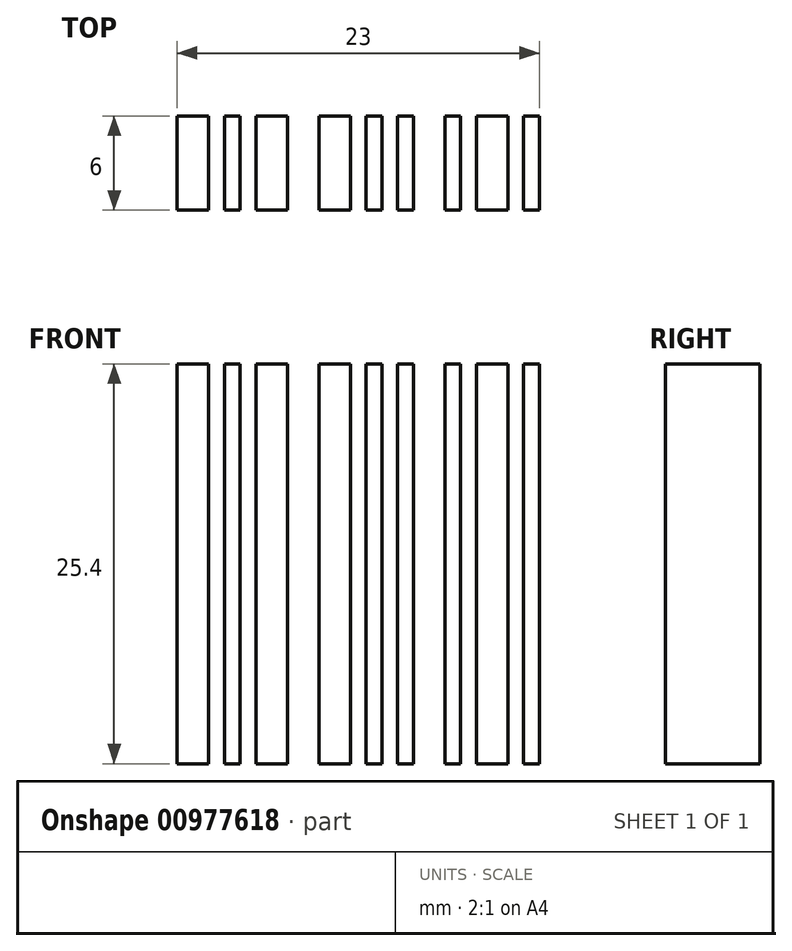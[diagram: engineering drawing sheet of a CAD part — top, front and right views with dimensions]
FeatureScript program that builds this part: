
annotation { "Feature Type Name" : "Feature", "Feature Type Description" : "" }
export const myFeature = defineFeature(function(context is Context, id is Id, definition is map)
    precondition{}
    {
        {
            var Q0;
            Q0=qCreatedBy(makeId("Top.planeOp"),FACE);
            var sketch = newSketch(context, id + "F0", { "sketchPlane" : qUnion([Q0])});
            skLineSegment(sketch, "E0.bottom", {"start": v(0, 0) * mm, "end": v(2, 0) * mm});
            skLineSegment(sketch, "E0.top", {"start": v(0, 6) * mm, "end": v(2, 6) * mm});
            skLineSegment(sketch, "E0.left", {"start": v(0, 0) * mm, "end": v(0, 6) * mm});
            skLineSegment(sketch, "E0.right", {"start": v(2, 0) * mm, "end": v(2, 6) * mm});
            skLineSegment(sketch, "E1", {"start": v(0, -3.5) * mm, "end": v(3, -3.5) * mm});
            skLineSegment(sketch, "E2", {"start": v(3, -3.5) * mm, "end": v(4, -3.5) * mm});
            skLineSegment(sketch, "E3", {"start": v(4, -3.5) * mm, "end": v(5, -3.5) * mm});
            skLineSegment(sketch, "E4", {"start": v(5, -3.5) * mm, "end": v(7, -3.5) * mm});
            skLineSegment(sketch, "E5", {"start": v(7, -3.5) * mm, "end": v(9, -3.5) * mm});
            skLineSegment(sketch, "E6.bottom", {"start": v(3, 0) * mm, "end": v(4, 0) * mm});
            skLineSegment(sketch, "E6.top", {"start": v(3, 6) * mm, "end": v(4, 6) * mm});
            skLineSegment(sketch, "E6.left", {"start": v(3, 0) * mm, "end": v(3, 6) * mm});
            skLineSegment(sketch, "E6.right", {"start": v(4, 0) * mm, "end": v(4, 6) * mm});
            skLineSegment(sketch, "E7.bottom", {"start": v(5, 0) * mm, "end": v(7, 0) * mm});
            skLineSegment(sketch, "E7.top", {"start": v(5, 6) * mm, "end": v(7, 6) * mm});
            skLineSegment(sketch, "E7.left", {"start": v(5, 0) * mm, "end": v(5, 6) * mm});
            skLineSegment(sketch, "E7.right", {"start": v(7, 0) * mm, "end": v(7, 6) * mm});
            skLineSegment(sketch, "E8.bottom", {"start": v(9, 0) * mm, "end": v(9, 0) * mm});
            skLineSegment(sketch, "E9.bottom", {"start": v(9, -3.5) * mm, "end": v(11, -3.5) * mm});
            skLineSegment(sketch, "E9.top", {"start": v(9, -3.5) * mm, "end": v(11, -3.5) * mm});
            skLineSegment(sketch, "E9.left", {"start": v(9, -3.5) * mm, "end": v(9, -3.5) * mm});
            skLineSegment(sketch, "E9.right", {"start": v(11, -3.5) * mm, "end": v(11, -3.5) * mm});
            skLineSegment(sketch, "E10.bottom", {"start": v(11, -3.5) * mm, "end": v(12, -3.5) * mm});
            skLineSegment(sketch, "E10.top", {"start": v(11, -3.5) * mm, "end": v(12, -3.5) * mm});
            skLineSegment(sketch, "E10.right", {"start": v(12, -3.5) * mm, "end": v(12, -3.5) * mm});
            skLineSegment(sketch, "E11.bottom", {"start": v(12, -3.5) * mm, "end": v(13, -3.5) * mm});
            skLineSegment(sketch, "E11.top", {"start": v(12, -3.5) * mm, "end": v(13, -3.5) * mm});
            skLineSegment(sketch, "E11.right", {"start": v(13, -3.5) * mm, "end": v(13, -3.5) * mm});
            skLineSegment(sketch, "E12.bottom", {"start": v(13, -3.5) * mm, "end": v(14, -3.5) * mm});
            skLineSegment(sketch, "E12.top", {"start": v(13, -3.5) * mm, "end": v(14, -3.5) * mm});
            skLineSegment(sketch, "E12.right", {"start": v(14, -3.5) * mm, "end": v(14, -3.5) * mm});
            skLineSegment(sketch, "E13.bottom", {"start": v(9, 0) * mm, "end": v(11, 0) * mm});
            skLineSegment(sketch, "E13.top", {"start": v(9, 6) * mm, "end": v(11, 6) * mm});
            skLineSegment(sketch, "E13.left", {"start": v(9, 0) * mm, "end": v(9, 6) * mm});
            skLineSegment(sketch, "E13.right", {"start": v(11, 0) * mm, "end": v(11, 6) * mm});
            skLineSegment(sketch, "E14.bottom", {"start": v(12, 0) * mm, "end": v(13, 0) * mm});
            skLineSegment(sketch, "E14.top", {"start": v(12, 6) * mm, "end": v(13, 6) * mm});
            skLineSegment(sketch, "E14.left", {"start": v(12, 0) * mm, "end": v(12, 6) * mm});
            skLineSegment(sketch, "E14.right", {"start": v(13, 0) * mm, "end": v(13, 6) * mm});
            skLineSegment(sketch, "E15.bottom", {"start": v(14, 0) * mm, "end": v(14, 0) * mm});
            skLineSegment(sketch, "E15.top", {"start": v(14, 6) * mm, "end": v(14, 6) * mm});
            skLineSegment(sketch, "E15.left", {"start": v(14, 0) * mm, "end": v(14, 6) * mm});
            skLineSegment(sketch, "E15.right", {"start": v(14, 0) * mm, "end": v(14, 6) * mm});
            skLineSegment(sketch, "E16.bottom", {"start": v(14, 6) * mm, "end": v(15, 6) * mm});
            skLineSegment(sketch, "E16.top", {"start": v(14, 0) * mm, "end": v(15, 0) * mm});
            skLineSegment(sketch, "E16.left", {"start": v(14, 6) * mm, "end": v(14, 0) * mm});
            skLineSegment(sketch, "E16.right", {"start": v(15, 6) * mm, "end": v(15, 0) * mm});
            skLineSegment(sketch, "E17", {"start": v(14, -3.5) * mm, "end": v(15, -3.5) * mm});
            skLineSegment(sketch, "E18", {"start": v(15, -3.5) * mm, "end": v(17, -3.5) * mm});
            skLineSegment(sketch, "E19", {"start": v(17, -3.5) * mm, "end": v(18, -3.5) * mm});
            skLineSegment(sketch, "E20", {"start": v(19, -3.5) * mm, "end": v(18, -3.5) * mm});
            skLineSegment(sketch, "E21", {"start": v(19, -3.5) * mm, "end": v(21, -3.5) * mm});
            skLineSegment(sketch, "E22", {"start": v(22, -3.5) * mm, "end": v(21, -3.5) * mm});
            skLineSegment(sketch, "E23", {"start": v(22, -3.5) * mm, "end": v(23, -3.5) * mm});
            skLineSegment(sketch, "E24.bottom", {"start": v(17, 0) * mm, "end": v(18, 0) * mm});
            skLineSegment(sketch, "E24.top", {"start": v(17, 6) * mm, "end": v(18, 6) * mm});
            skLineSegment(sketch, "E24.left", {"start": v(17, 0) * mm, "end": v(17, 6) * mm});
            skLineSegment(sketch, "E24.right", {"start": v(18, 0) * mm, "end": v(18, 6) * mm});
            skLineSegment(sketch, "E25.bottom", {"start": v(19, 0) * mm, "end": v(21, 0) * mm});
            skLineSegment(sketch, "E25.top", {"start": v(19, 6) * mm, "end": v(21, 6) * mm});
            skLineSegment(sketch, "E25.left", {"start": v(19, 0) * mm, "end": v(19, 6) * mm});
            skLineSegment(sketch, "E25.right", {"start": v(21, 0) * mm, "end": v(21, 6) * mm});
            skLineSegment(sketch, "E26.bottom", {"start": v(22, 0) * mm, "end": v(23, 0) * mm});
            skLineSegment(sketch, "E26.top", {"start": v(22, 6) * mm, "end": v(23, 6) * mm});
            skLineSegment(sketch, "E26.left", {"start": v(22, 0) * mm, "end": v(22, 6) * mm});
            skLineSegment(sketch, "E26.right", {"start": v(23, 0) * mm, "end": v(23, 6) * mm});
            skSolve(sketch);
        }
        {
            var Q0;
            Q0 = qSketchRegion(id + "F0", true);
            extrude(context, id + "F1", {"entities" : qUnion([Q0]), "depth" : 25.4 * mm, "offsetDistance" : 25.4 * mm});
        }
    });
